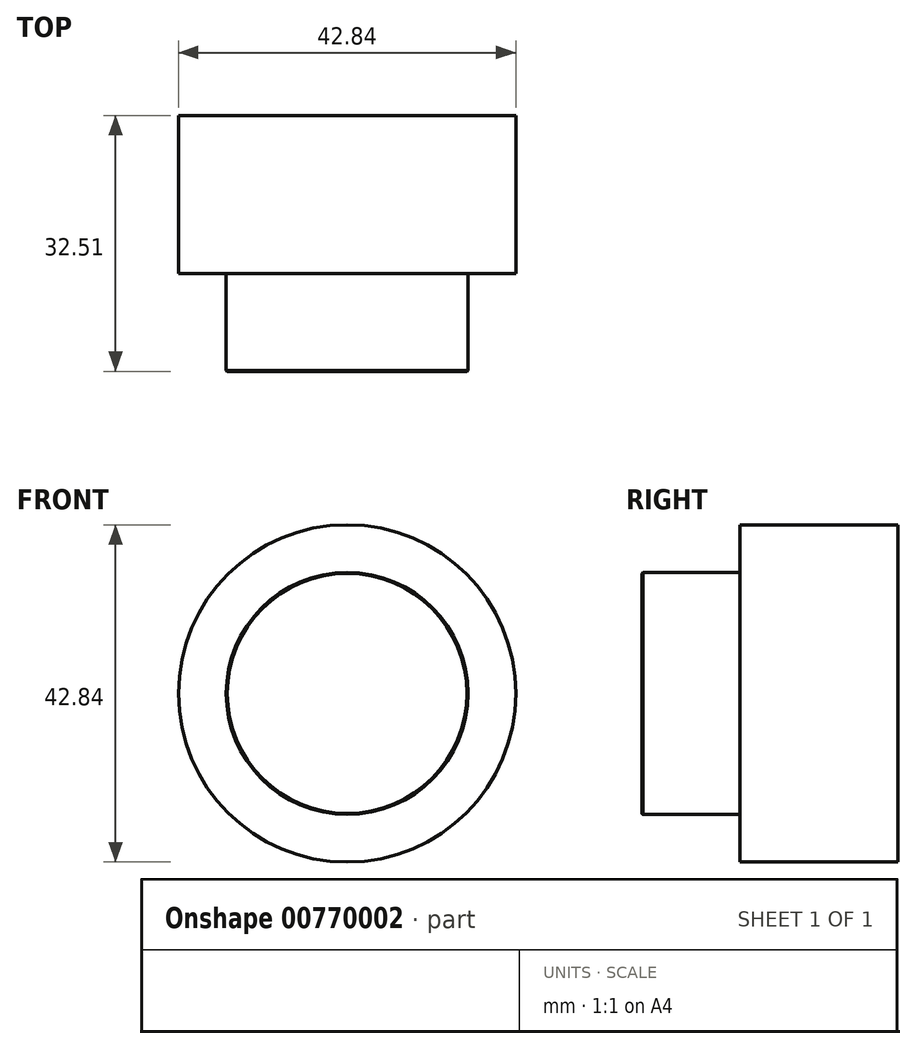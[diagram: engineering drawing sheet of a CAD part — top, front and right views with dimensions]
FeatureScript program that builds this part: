
annotation { "Feature Type Name" : "Feature", "Feature Type Description" : "" }
export const myFeature = defineFeature(function(context is Context, id is Id, definition is map)
    precondition{}
    {
        {
            var Q0;
            Q0=qCreatedBy(makeId("Front.planeOp"),FACE);
            var sketch = newSketch(context, id + "F0", { "sketchPlane" : qUnion([Q0])});
            skCircle(sketch, "E0", {"center": v(0, 0) * mm, "radius": 21.42 * mm});
            skCircle(sketch, "E1", {"center": v(0, 0) * mm, "radius": 15.37 * mm});
            skSolve(sketch);
        }
        {
            var Q0;
            Q0 = qSketchRegion(id + "F0", true);
            var Q1;
            Q1=makeQuery(id+"F0.imprint","IMPRINT",FACE,{"disambiguationData":[TD([[makeQuery(id+"F0.imprint","IMPRINT",EDGE,{"derivedFrom":sQuery(id+"F0.wireOp",EDGE,"E1")}),1.0]])]});
            extrude(context, id + "F1", {"entities" : qUnion([Q0, Q1]), "depth" : 20.07 * mm, "offsetDistance" : 25.4 * mm});
        }
        {
            var Q0;
            Q0=qCreatedBy(makeId("Front.planeOp"),FACE);
            var sketch = newSketch(context, id + "F2", { "sketchPlane" : qUnion([Q0])});
            skCircle(sketch, "E2", {"center": v(0, 0) * mm, "radius": 15.37 * mm});
            skSolve(sketch);
        }
        {
            var Q0;
            Q0 = qSketchRegion(id + "F2", true);
            extrude(context, id + "F3", {"entities" : qUnion([Q0]), "operationType" : NewBodyOperationType.ADD, "depth" : 32.5 * mm, "offsetDistance" : 25.4 * mm});
        }
        {
            var Q0;
            Q0=makeQuery(id+"F3.opExtrude","CAP_EDGE",EDGE,{"disambiguationData":[OSD([sQuery(id+"F2.wireOp",EDGE,"E2")])],"isStart":false});
            chamfer(context, id + "F4", {"entities" : qUnion([Q0]), "chamferType" : ChamferType.TWO_OFFSETS, "width1" : 0.13 * mm, "oppositeDirection" : false, "width2" : 0.13 * mm, "tangentPropagation" : true});
        }
    });
